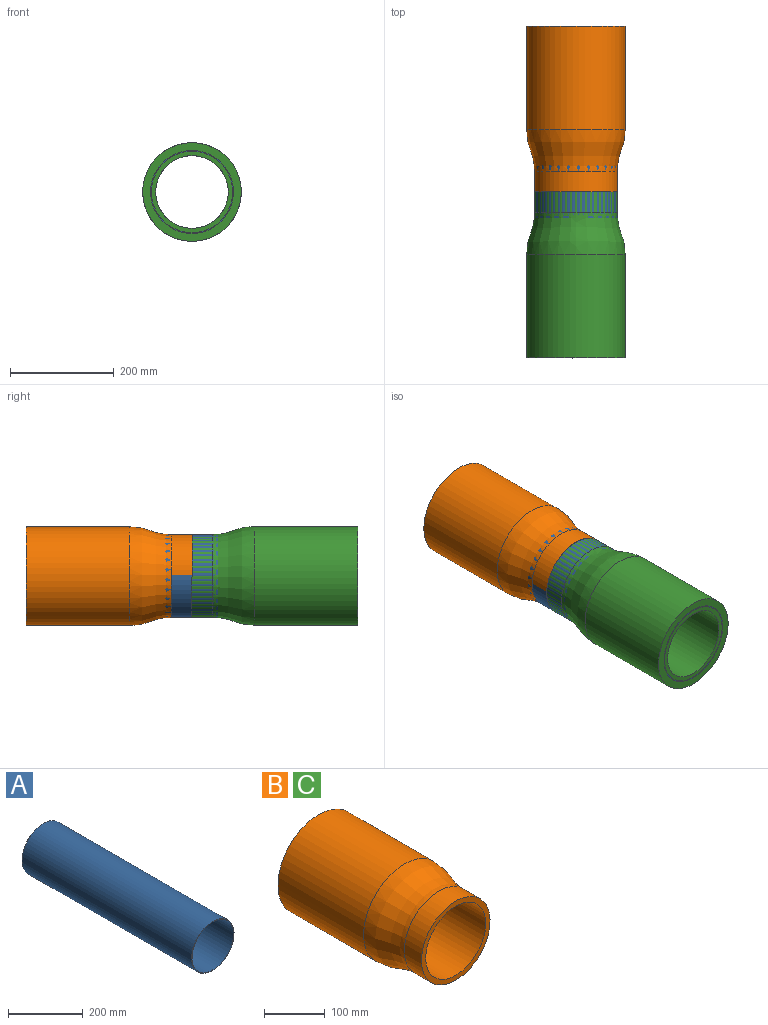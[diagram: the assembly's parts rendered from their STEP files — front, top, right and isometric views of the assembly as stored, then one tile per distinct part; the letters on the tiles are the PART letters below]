
ASSEMBLY  parts=3 mates=1
PART A: 4 faces, bbox 160x640x160 mm
  f0: cylinder r=78.5mm len=640mm, axis (0,1,0), area 315667.2mm2, adj f2,f3
  f1: cylinder r=80mm len=640mm, axis (0,1,0), area 321699.1mm2, adj f2,f3
  f2: plane 160x160mm, normal (0,-1,0), area 746.9mm2, adj f0,f1
  f3: plane 160x160mm, normal (0,1,0), area 746.9mm2, adj f0,f1
PART B: 6 faces, bbox 190x320x190 mm
  f0: plane 190x190mm, normal (0,1,0), area 12959.1mm2, adj f1,f5
  f1: cylinder r=95mm len=200mm, axis (0,-1,0), area 119380.5mm2, adj f0,f2
  f2: revolved ~190x190mm, area 45058.4mm2, adj f1,f3
  f3: cylinder r=80mm len=160mm, axis (0,-1,0), area 20106.2mm2, adj f2,f4
  f4: plane 160x160mm, normal (0,-1,0), area 4712.4mm2, adj f3,f5
  f5: cylinder r=70mm len=320mm, axis (0,-1,0), area 140743.4mm2, adj f0,f4
PART C: same geometry as B
PLACE A rot(axis=(1,-0.03,0.03),0deg) t=(75.31,-658.03,8.23)mm fixed
PLACE B rot(axis=(1,-0.03,0.03),0deg) t=(75.31,-898.03,19.49)mm
PLACE C rot(axis=(-1,0,0),180deg) t=(75.31,-1058.03,-3.02)mm
MATE revolute C.f1 <-> A.f0  axis (0,-1,0) through (75.31,-1298.03,8.23)mm
